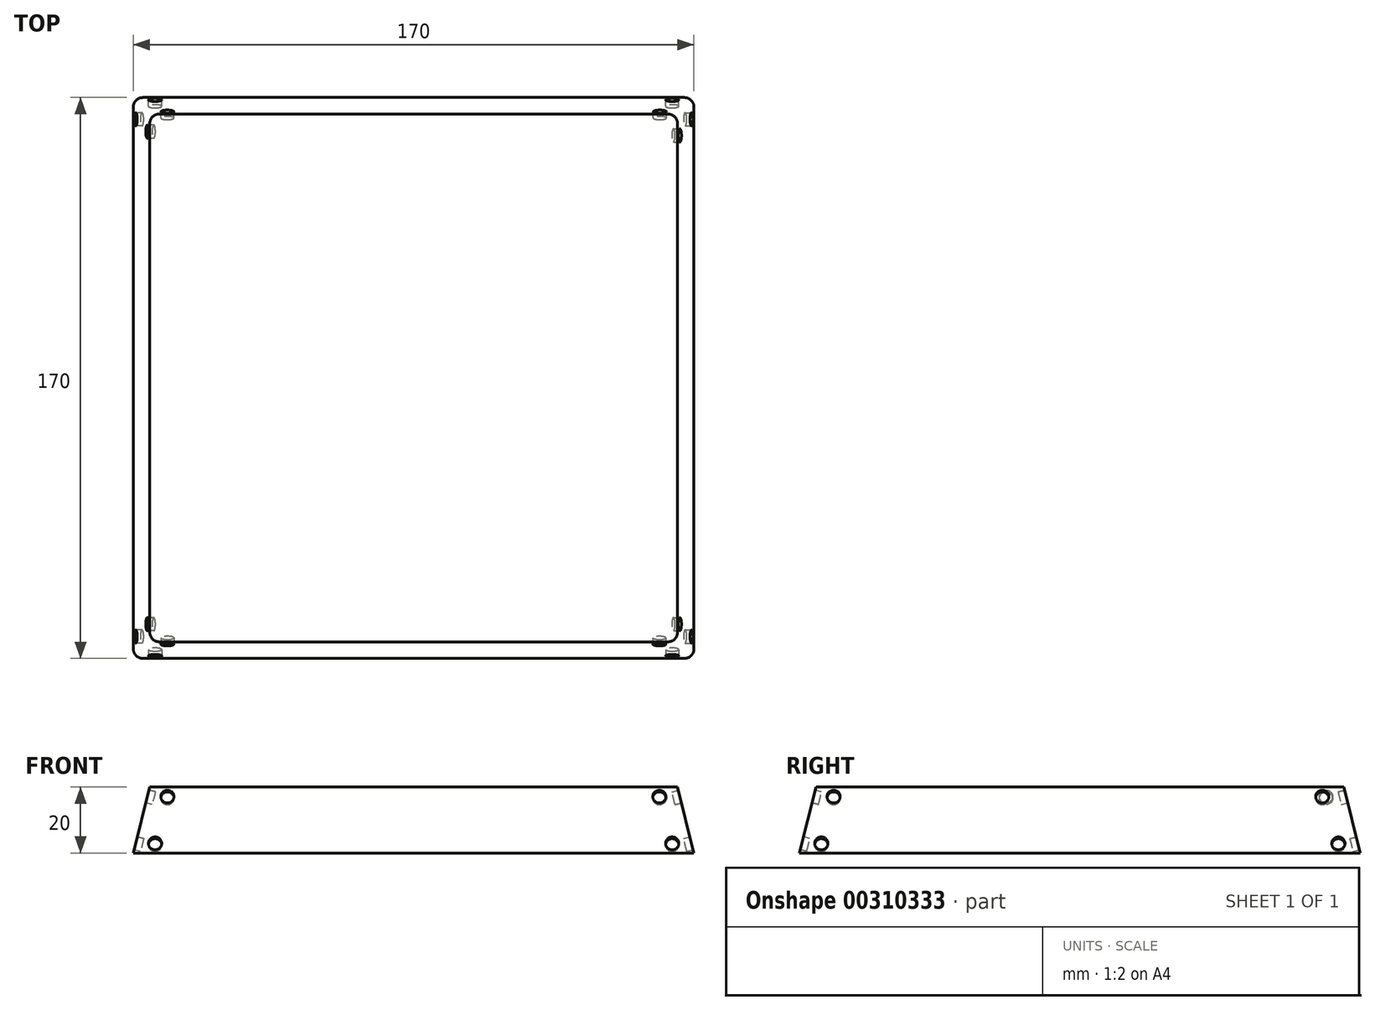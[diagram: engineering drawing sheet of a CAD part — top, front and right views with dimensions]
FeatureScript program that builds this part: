
annotation { "Feature Type Name" : "Feature", "Feature Type Description" : "" }
export const myFeature = defineFeature(function(context is Context, id is Id, definition is map)
    precondition{}
    {
        {
            var Q0;
            Q0=qCreatedBy(makeId("Top.planeOp"),FACE);
            var sketch = newSketch(context, id + "F0", { "sketchPlane" : qUnion([Q0])});
            skLineSegment(sketch, "E0.bottom", {"start": v(-85, 85) * mm, "end": v(85, 85) * mm});
            skLineSegment(sketch, "E0.top", {"start": v(-85, -85) * mm, "end": v(85, -85) * mm});
            skLineSegment(sketch, "E0.left", {"start": v(-85, 85) * mm, "end": v(-85, -85) * mm});
            skLineSegment(sketch, "E0.right", {"start": v(85, 85) * mm, "end": v(85, -85) * mm});
            skSolve(sketch);
        }
        {
            var Q0;
            Q0=makeQuery(id+"F0.imprint","IMPRINT",FACE,{"disambiguationData":[TD([[makeQuery(id+"F0.imprint","IMPRINT",EDGE,{"derivedFrom":sQuery(id+"F0.wireOp",EDGE,"E0.bottom")}),-1.0]])]});
            cPlane(context, id + "F1", {"entities" : qUnion([Q0]), "cplaneType" : CPlaneType.OFFSET, "offset" : 20 * mm, "width" : 150 * mm, "height" : 150 * mm});
        }
        {
            var Q0;
            Q0=qCreatedBy(id+"F1.planeOp",FACE);
            var sketch = newSketch(context, id + "F2", { "sketchPlane" : qUnion([Q0])});
            skLineSegment(sketch, "E1.bottom", {"start": v(-80, 80) * mm, "end": v(80, 80) * mm});
            skLineSegment(sketch, "E1.top", {"start": v(-80, -80) * mm, "end": v(80, -80) * mm});
            skLineSegment(sketch, "E1.left", {"start": v(-80, 80) * mm, "end": v(-80, -80) * mm});
            skLineSegment(sketch, "E1.right", {"start": v(80, 80) * mm, "end": v(80, -80) * mm});
            skSolve(sketch);
        }
        {
            var Q0;
            Q0=makeQuery(id+"F0.imprint","IMPRINT",FACE,{"disambiguationData":[TD([[makeQuery(id+"F0.imprint","IMPRINT",EDGE,{"derivedFrom":sQuery(id+"F0.wireOp",EDGE,"E0.bottom")}),-1.0]])]});
            var Q1;
            Q1=makeQuery(id+"F2.imprint","IMPRINT",FACE,{"disambiguationData":[TD([[makeQuery(id+"F2.imprint","IMPRINT",EDGE,{"derivedFrom":sQuery(id+"F2.wireOp",EDGE,"E1.bottom")}),-1.0]])]});
            loft(context, id + "F3", {"sheetProfilesArray" : [{ "sheetProfileEntities" : qUnion([Q0]) }, { "sheetProfileEntities" : qUnion([Q1]) }]});
        }
        {
            var Q0;
            Q0=makeQuery(id+"F3.opLoft","SWEPT_EDGE",EDGE,{"disambiguationData":[OSD([sQuery(id+"F0.wireOp",EDGE,"E0.top"),sQuery(id+"F0.wireOp",EDGE,"E0.right"),sQuery(id+"F2.wireOp",EDGE,"E1.top"),sQuery(id+"F2.wireOp",EDGE,"E1.right")])]});
            fillet(context, id + "F4", {"entities" : qUnion([Q0]), "radius" : 3 * mm, "tangentPropagation" : true, "allowEdgeOverflow" : false});
        }
        {
            var Q0;
            Q0=makeQuery(id+"F3.opLoft","SWEPT_EDGE",EDGE,{"disambiguationData":[OSD([sQuery(id+"F0.wireOp",EDGE,"E0.top"),sQuery(id+"F0.wireOp",EDGE,"E0.left"),sQuery(id+"F2.wireOp",EDGE,"E1.top"),sQuery(id+"F2.wireOp",EDGE,"E1.left")])]});
            var Q1;
            Q1=makeQuery(id+"F3.opLoft","SWEPT_EDGE",EDGE,{"disambiguationData":[OSD([sQuery(id+"F0.wireOp",EDGE,"E0.bottom"),sQuery(id+"F0.wireOp",EDGE,"E0.left"),sQuery(id+"F2.wireOp",EDGE,"E1.bottom"),sQuery(id+"F2.wireOp",EDGE,"E1.left")])]});
            var Q2;
            Q2=makeQuery(id+"F3.opLoft","SWEPT_EDGE",EDGE,{"disambiguationData":[OSD([sQuery(id+"F0.wireOp",EDGE,"E0.bottom"),sQuery(id+"F0.wireOp",EDGE,"E0.right"),sQuery(id+"F2.wireOp",EDGE,"E1.bottom"),sQuery(id+"F2.wireOp",EDGE,"E1.right")])]});
            fillet(context, id + "F5", {"entities" : qUnion([Q0, Q1, Q2]), "radius" : 3 * mm, "tangentPropagation" : true, "allowEdgeOverflow" : false});
        }
        {
            var Q0;
            Q0=makeQuery(id+"F3.opLoft","SWEPT_FACE",FACE,{"disambiguationData":[OSD([sQuery(id+"F0.wireOp",EDGE,"E0.top"),sQuery(id+"F0.wireOp",EDGE,"E0.left"),sQuery(id+"F0.wireOp",EDGE,"E0.right"),sQuery(id+"F2.wireOp",EDGE,"E1.top"),sQuery(id+"F2.wireOp",EDGE,"E1.left"),sQuery(id+"F2.wireOp",EDGE,"E1.right")])]});
            var sketch = newSketch(context, id + "F6", { "sketchPlane" : qUnion([Q0])});
            skSolve(sketch);
        }
        {
            var Q0;
            {var subQ3=sQuery(id+"F0.wireOp",EDGE,"E0.right");var subQ4=sQuery(id+"F0.wireOp",EDGE,"E0.left");var subQ5=sQuery(id+"F0.wireOp",EDGE,"E0.top");Q0=makeQuery(id+"F6.imprint","IMPRINT",FACE,{"disambiguationData":[TD([[makeQuery(id+"F6.imprint","IMPRINT",EDGE,{"derivedFrom":makeQuery(id+"F3.opLoft","MID_CAP_EDGE",EDGE,{"disambiguationData":[OSD([subQ5,subQ4,subQ3])],"capPos":0.0})}),1.0]])]});}
            var sketch = newSketch(context, id + "F7", { "sketchPlane" : qUnion([Q0])});
            skLineSegment(sketch, "E2", {"start": v(-73.55, -6.62) * mm, "end": v(-75.66, -15.33) * mm});
            skLineSegment(sketch, "E3", {"start": v(-23.7, -17.8) * mm, "end": v(-23.7, -2.8) * mm});
            skLineSegment(sketch, "E4", {"start": v(-23.7, -2.8) * mm, "end": v(-68.7, -2.8) * mm});
            skLineSegment(sketch, "E5", {"start": v(-73.72, -17.8) * mm, "end": v(-23.7, -17.8) * mm});
            skPoint(sketch, "E6.visualSharp", {"position": v(-72.62, -2.8) * mm});
            skArc(sketch, "E6.filletArc", {"start": v(-68.7, -2.8) * mm, "mid": v(-71.78, -3.87) * mm, "end": v(-73.55, -6.62) * mm});
            skPoint(sketch, "E7.visualSharp", {"position": v(-76.26, -17.8) * mm});
            skArc(sketch, "E7.filletArc", {"start": v(-75.66, -15.33) * mm, "mid": v(-75.3, -17.04) * mm, "end": v(-73.72, -17.8) * mm});
            skPoint(sketch, "E8.visualSharp", {"position": v(72.62, -2.8) * mm});
            skPoint(sketch, "E9.visualSharp", {"position": v(76.27, -17.82) * mm});
            skLineSegment(sketch, "E10.MirrorCS", {"start": v(23.7, -2.8) * mm, "end": v(68.7, -2.8) * mm});
            skArc(sketch, "E11.MirrorCS", {"start": v(68.7, -2.8) * mm, "mid": v(71.78, -3.87) * mm, "end": v(73.55, -6.62) * mm});
            skLineSegment(sketch, "E12.MirrorCS", {"start": v(73.55, -6.62) * mm, "end": v(75.66, -15.33) * mm});
            skArc(sketch, "E13.MirrorCS", {"start": v(75.66, -15.33) * mm, "mid": v(75.3, -17.04) * mm, "end": v(73.72, -17.8) * mm});
            skLineSegment(sketch, "E14.MirrorCS", {"start": v(73.72, -17.8) * mm, "end": v(23.7, -17.8) * mm});
            skLineSegment(sketch, "E15.MirrorCS", {"start": v(23.7, -17.8) * mm, "end": v(23.7, -2.8) * mm});
            skLineSegment(sketch, "E16.bottom", {"start": v(-19.7, -2.8) * mm, "end": v(19.7, -2.8) * mm});
            skLineSegment(sketch, "E16.top", {"start": v(-19.7, -17.8) * mm, "end": v(19.7, -17.8) * mm});
            skLineSegment(sketch, "E16.left", {"start": v(-19.7, -2.8) * mm, "end": v(-19.7, -17.8) * mm});
            skLineSegment(sketch, "E16.right", {"start": v(19.7, -2.8) * mm, "end": v(19.7, -17.8) * mm});
            skSolve(sketch);
        }
        {
            var Q0;
            Q0=makeQuery(id+"F3.opLoft","SWEPT_FACE",FACE,{"disambiguationData":[OSD([sQuery(id+"F0.wireOp",EDGE,"E0.bottom"),sQuery(id+"F0.wireOp",EDGE,"E0.top"),sQuery(id+"F0.wireOp",EDGE,"E0.right"),sQuery(id+"F2.wireOp",EDGE,"E1.bottom"),sQuery(id+"F2.wireOp",EDGE,"E1.top"),sQuery(id+"F2.wireOp",EDGE,"E1.right")])]});
            var sketch = newSketch(context, id + "F8", { "sketchPlane" : qUnion([Q0])});
            skLineSegment(sketch, "E17", {"start": v(-73.55, -6.62) * mm, "end": v(-75.66, -15.33) * mm});
            skLineSegment(sketch, "E18", {"start": v(-23.7, -17.8) * mm, "end": v(-23.7, -2.8) * mm});
            skLineSegment(sketch, "E19", {"start": v(-23.7, -2.8) * mm, "end": v(-68.7, -2.8) * mm});
            skLineSegment(sketch, "E20", {"start": v(-73.72, -17.8) * mm, "end": v(-23.7, -17.8) * mm});
            skPoint(sketch, "E21.visualSharp", {"position": v(-72.62, -2.8) * mm});
            skArc(sketch, "E21.filletArc", {"start": v(-68.7, -2.8) * mm, "mid": v(-71.78, -3.87) * mm, "end": v(-73.55, -6.62) * mm});
            skPoint(sketch, "E22.visualSharp", {"position": v(-76.26, -17.8) * mm});
            skArc(sketch, "E22.filletArc", {"start": v(-75.66, -15.33) * mm, "mid": v(-75.3, -17.04) * mm, "end": v(-73.72, -17.8) * mm});
            skPoint(sketch, "E23.visualSharp", {"position": v(73.2, -2.72) * mm});
            skPoint(sketch, "E24.visualSharp", {"position": v(76.85, -17.73) * mm});
            skLineSegment(sketch, "E25.MirrorCS", {"start": v(24.28, -2.8) * mm, "end": v(69.28, -2.8) * mm});
            skArc(sketch, "E26.MirrorCS", {"start": v(69.28, -2.72) * mm, "mid": v(72.37, -3.79) * mm, "end": v(74.14, -6.54) * mm});
            skLineSegment(sketch, "E27.MirrorCS", {"start": v(74.14, -6.54) * mm, "end": v(76.25, -15.24) * mm});
            skArc(sketch, "E28.MirrorCS", {"start": v(76.25, -15.24) * mm, "mid": v(75.88, -16.95) * mm, "end": v(74.3, -17.72) * mm});
            skLineSegment(sketch, "E29.MirrorCS", {"start": v(74.3, -17.72) * mm, "end": v(24.28, -17.72) * mm});
            skLineSegment(sketch, "E30.MirrorCS", {"start": v(24.28, -17.8) * mm, "end": v(24.28, -2.8) * mm});
            skLineSegment(sketch, "E31.bottom", {"start": v(-19.7, -2.8) * mm, "end": v(20.28, -2.8) * mm});
            skLineSegment(sketch, "E31.top", {"start": v(-19.7, -17.8) * mm, "end": v(20.28, -17.8) * mm});
            skLineSegment(sketch, "E31.left", {"start": v(-19.7, -2.8) * mm, "end": v(-19.7, -17.8) * mm});
            skLineSegment(sketch, "E31.right", {"start": v(20.28, -2.8) * mm, "end": v(20.28, -17.8) * mm});
            skSolve(sketch);
        }
        {
            var Q0;
            Q0=makeQuery(id+"F3.opLoft","SWEPT_FACE",FACE,{"disambiguationData":[OSD([sQuery(id+"F0.wireOp",EDGE,"E0.bottom"),sQuery(id+"F0.wireOp",EDGE,"E0.top"),sQuery(id+"F0.wireOp",EDGE,"E0.left"),sQuery(id+"F2.wireOp",EDGE,"E1.bottom"),sQuery(id+"F2.wireOp",EDGE,"E1.top"),sQuery(id+"F2.wireOp",EDGE,"E1.left")])]});
            var sketch = newSketch(context, id + "F9", { "sketchPlane" : qUnion([Q0])});
            skLineSegment(sketch, "E32", {"start": v(-74.18, -6.62) * mm, "end": v(-76.3, -15.33) * mm});
            skLineSegment(sketch, "E33", {"start": v(-24.32, -17.8) * mm, "end": v(-24.32, -2.8) * mm});
            skLineSegment(sketch, "E34", {"start": v(-24.32, -2.8) * mm, "end": v(-69.32, -2.8) * mm});
            skLineSegment(sketch, "E35", {"start": v(-74.35, -17.8) * mm, "end": v(-24.32, -17.8) * mm});
            skPoint(sketch, "E36.visualSharp", {"position": v(-73.25, -2.8) * mm});
            skArc(sketch, "E36.filletArc", {"start": v(-69.32, -2.8) * mm, "mid": v(-72.41, -3.87) * mm, "end": v(-74.18, -6.62) * mm});
            skPoint(sketch, "E37.visualSharp", {"position": v(-76.9, -17.8) * mm});
            skArc(sketch, "E37.filletArc", {"start": v(-76.3, -15.33) * mm, "mid": v(-75.92, -17.04) * mm, "end": v(-74.35, -17.8) * mm});
            skLineSegment(sketch, "E38.MirrorCS", {"start": v(23.7, -2.8) * mm, "end": v(68.7, -2.8) * mm});
            skLineSegment(sketch, "E39.MirrorCS", {"start": v(73.72, -17.78) * mm, "end": v(23.7, -17.78) * mm});
            skLineSegment(sketch, "E40.MirrorCS", {"start": v(23.7, -17.8) * mm, "end": v(23.7, -2.8) * mm});
            skLineSegment(sketch, "E41.bottom", {"start": v(-20.32, -2.8) * mm, "end": v(19.7, -2.8) * mm});
            skLineSegment(sketch, "E41.top", {"start": v(-20.32, -17.8) * mm, "end": v(19.7, -17.8) * mm});
            skLineSegment(sketch, "E41.left", {"start": v(-20.32, -2.8) * mm, "end": v(-20.32, -17.8) * mm});
            skLineSegment(sketch, "E41.right", {"start": v(19.7, -2.8) * mm, "end": v(19.7, -17.8) * mm});
            skLineSegment(sketch, "E42", {"start": v(73.5, -6.47) * mm, "end": v(75.7, -15.27) * mm});
            skArc(sketch, "E43", {"start": v(73.72, -17.78) * mm, "mid": v(75.32, -17.01) * mm, "end": v(75.7, -15.27) * mm});
            skArc(sketch, "E44", {"start": v(73.5, -6.47) * mm, "mid": v(71.72, -3.82) * mm, "end": v(68.7, -2.8) * mm});
            skSolve(sketch);
        }
        {
            var Q0;
            Q0=makeQuery(id+"F3.opLoft","SWEPT_FACE",FACE,{"disambiguationData":[OSD([sQuery(id+"F0.wireOp",EDGE,"E0.bottom"),sQuery(id+"F0.wireOp",EDGE,"E0.left"),sQuery(id+"F0.wireOp",EDGE,"E0.right"),sQuery(id+"F2.wireOp",EDGE,"E1.bottom"),sQuery(id+"F2.wireOp",EDGE,"E1.left"),sQuery(id+"F2.wireOp",EDGE,"E1.right")])]});
            var sketch = newSketch(context, id + "F10", { "sketchPlane" : qUnion([Q0])});
            skLineSegment(sketch, "E45", {"start": v(-73.54, -6.6) * mm, "end": v(-75.65, -15.32) * mm});
            skLineSegment(sketch, "E46", {"start": v(-23.68, -17.79) * mm, "end": v(-23.68, -2.79) * mm});
            skLineSegment(sketch, "E47", {"start": v(-23.68, -2.79) * mm, "end": v(-68.68, -2.79) * mm});
            skLineSegment(sketch, "E48", {"start": v(-73.71, -17.79) * mm, "end": v(-23.68, -17.79) * mm});
            skPoint(sketch, "E49.visualSharp", {"position": v(-72.62, -2.79) * mm});
            skArc(sketch, "E49.filletArc", {"start": v(-68.68, -2.79) * mm, "mid": v(-71.77, -3.86) * mm, "end": v(-73.54, -6.6) * mm});
            skPoint(sketch, "E50.visualSharp", {"position": v(-76.25, -17.79) * mm});
            skArc(sketch, "E50.filletArc", {"start": v(-75.65, -15.32) * mm, "mid": v(-75.28, -17.02) * mm, "end": v(-73.71, -17.79) * mm});
            skPoint(sketch, "E51.visualSharp", {"position": v(72.63, -2.79) * mm});
            skPoint(sketch, "E52.visualSharp", {"position": v(76.27, -17.8) * mm});
            skLineSegment(sketch, "E53.MirrorCS", {"start": v(23.7, -2.79) * mm, "end": v(68.7, -2.79) * mm});
            skArc(sketch, "E54.MirrorCS", {"start": v(68.7, -2.79) * mm, "mid": v(71.8, -3.86) * mm, "end": v(73.56, -6.6) * mm});
            skLineSegment(sketch, "E55.MirrorCS", {"start": v(73.56, -6.6) * mm, "end": v(75.67, -15.32) * mm});
            skArc(sketch, "E56.MirrorCS", {"start": v(75.67, -15.32) * mm, "mid": v(75.3, -17.02) * mm, "end": v(73.73, -17.79) * mm});
            skLineSegment(sketch, "E57.MirrorCS", {"start": v(73.73, -17.79) * mm, "end": v(23.7, -17.79) * mm});
            skLineSegment(sketch, "E58.MirrorCS", {"start": v(23.7, -17.79) * mm, "end": v(23.7, -2.79) * mm});
            skLineSegment(sketch, "E59.bottom", {"start": v(-19.68, -2.79) * mm, "end": v(19.7, -2.79) * mm});
            skLineSegment(sketch, "E59.top", {"start": v(-19.68, -17.79) * mm, "end": v(19.7, -17.79) * mm});
            skLineSegment(sketch, "E59.left", {"start": v(-19.68, -2.79) * mm, "end": v(-19.68, -17.79) * mm});
            skLineSegment(sketch, "E59.right", {"start": v(19.7, -2.79) * mm, "end": v(19.7, -17.79) * mm});
            skSolve(sketch);
        }
        {
            var Q0;
            Q0=makeQuery(id+"F8.imprint","IMPRINT",FACE,{"disambiguationData":[TD([[makeQuery(id+"F8.imprint","IMPRINT",EDGE,{"derivedFrom":sQuery(id+"F8.wireOp",EDGE,"E17")}),-1.0]])]});
            var sketch = newSketch(context, id + "F11", { "sketchPlane" : qUnion([Q0])});
            skCircle(sketch, "E60", {"center": v(-74.66, -3) * mm, "radius": 2 * mm});
            skCircle(sketch, "E61", {"center": v(-78.39, -17.62) * mm, "radius": 2 * mm});
            skCircle(sketch, "E62", {"center": v(73.5, -3) * mm, "radius": 2 * mm});
            skCircle(sketch, "E63", {"center": v(78.39, -17.62) * mm, "radius": 2 * mm});
            skSolve(sketch);
        }
        {
            var Q0;
            Q0 = qSketchRegion(id + "F11", true);
            extrude(context, id + "F12", {"entities" : qUnion([Q0]), "operationType" : NewBodyOperationType.REMOVE, "oppositeDirection" : true, "depth" : 2 * mm, "offsetDistance" : 25 * mm});
        }
        {
            var Q0;
            Q0=makeQuery(id+"F7.imprint","IMPRINT",FACE,{"disambiguationData":[TD([[makeQuery(id+"F7.imprint","IMPRINT",EDGE,{"derivedFrom":sQuery(id+"F7.wireOp",EDGE,"E2")}),-1.0]])]});
            var sketch = newSketch(context, id + "F13", { "sketchPlane" : qUnion([Q0])});
            skCircle(sketch, "E64", {"center": v(-74.66, -3) * mm, "radius": 2 * mm});
            skCircle(sketch, "E65", {"center": v(-78.39, -17.62) * mm, "radius": 2 * mm});
            skCircle(sketch, "E66", {"center": v(74.5, -3) * mm, "radius": 2 * mm});
            skCircle(sketch, "E67", {"center": v(78.39, -17.62) * mm, "radius": 2 * mm});
            skSolve(sketch);
        }
        {
            var Q0;
            Q0 = qSketchRegion(id + "F13", true);
            extrude(context, id + "F14", {"entities" : qUnion([Q0]), "operationType" : NewBodyOperationType.REMOVE, "oppositeDirection" : true, "depth" : 2 * mm, "offsetDistance" : 25 * mm});
        }
        {
            var Q0;
            Q0=makeQuery(id+"F9.imprint","IMPRINT",FACE,{"disambiguationData":[TD([[makeQuery(id+"F9.imprint","IMPRINT",EDGE,{"derivedFrom":sQuery(id+"F9.wireOp",EDGE,"E32")}),-1.0]])]});
            var sketch = newSketch(context, id + "F15", { "sketchPlane" : qUnion([Q0])});
            skCircle(sketch, "E68", {"center": v(-74.66, -3) * mm, "radius": 2 * mm});
            skCircle(sketch, "E69", {"center": v(-78.39, -17.62) * mm, "radius": 2 * mm});
            skCircle(sketch, "E70", {"center": v(74.66, -3) * mm, "radius": 2 * mm});
            skCircle(sketch, "E71", {"center": v(78.39, -17.62) * mm, "radius": 2 * mm});
            skSolve(sketch);
        }
        {
            var Q0;
            Q0 = qSketchRegion(id + "F11", true);
            extrude(context, id + "F16", {"entities" : qUnion([Q0]), "operationType" : NewBodyOperationType.REMOVE, "oppositeDirection" : true, "depth" : 2 * mm, "offsetDistance" : 25 * mm});
        }
        {
            var Q0;
            Q0 = qSketchRegion(id + "F15", true);
            extrude(context, id + "F17", {"entities" : qUnion([Q0]), "operationType" : NewBodyOperationType.REMOVE, "oppositeDirection" : true, "depth" : 2 * mm, "offsetDistance" : 25 * mm});
        }
        {
            var Q0;
            Q0=makeQuery(id+"F10.imprint","IMPRINT",FACE,{"disambiguationData":[TD([[makeQuery(id+"F10.imprint","IMPRINT",EDGE,{"derivedFrom":sQuery(id+"F10.wireOp",EDGE,"E45")}),-1.0]])]});
            var sketch = newSketch(context, id + "F18", { "sketchPlane" : qUnion([Q0])});
            skCircle(sketch, "E72", {"center": v(-74.66, -3) * mm, "radius": 2 * mm});
            skCircle(sketch, "E73", {"center": v(-78.39, -17.62) * mm, "radius": 2 * mm});
            skCircle(sketch, "E74", {"center": v(74.66, -3) * mm, "radius": 2 * mm});
            skCircle(sketch, "E75", {"center": v(78.39, -17.62) * mm, "radius": 2 * mm});
            skSolve(sketch);
        }
        {
            var Q0;
            Q0 = qSketchRegion(id + "F18", true);
            extrude(context, id + "F19", {"entities" : qUnion([Q0]), "operationType" : NewBodyOperationType.REMOVE, "oppositeDirection" : true, "depth" : 2 * mm, "offsetDistance" : 25 * mm});
        }
    });
